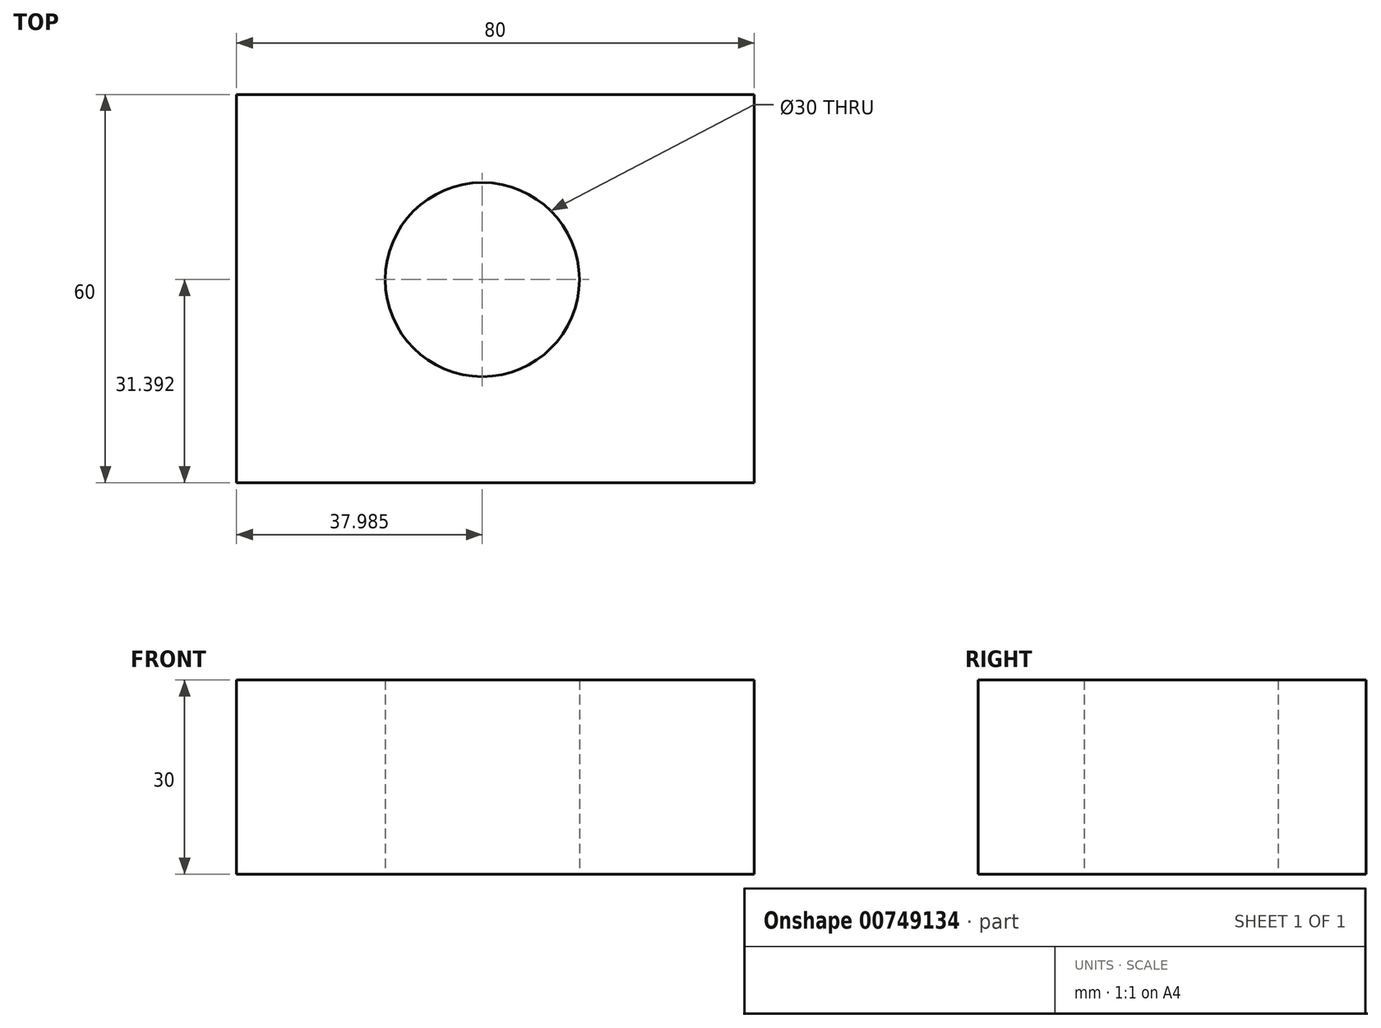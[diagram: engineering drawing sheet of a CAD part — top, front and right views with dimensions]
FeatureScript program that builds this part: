
annotation { "Feature Type Name" : "Feature", "Feature Type Description" : "" }
export const myFeature = defineFeature(function(context is Context, id is Id, definition is map)
    precondition{}
    {
        {
            var Q0;
            Q0=qCreatedBy(makeId("Top.planeOp"),FACE);
            var sketch = newSketch(context, id + "F0", { "sketchPlane" : qUnion([Q0])});
            skLineSegment(sketch, "E0", {"start": v(-63.1, 47.73) * mm, "end": v(-63.1, -12.27) * mm});
            skLineSegment(sketch, "E1", {"start": v(-63.1, -12.27) * mm, "end": v(16.9, -12.27) * mm});
            skLineSegment(sketch, "E2", {"start": v(16.9, -12.27) * mm, "end": v(16.9, 47.73) * mm});
            skLineSegment(sketch, "E3", {"start": v(16.9, 47.73) * mm, "end": v(-63.1, 47.73) * mm});
            skCircle(sketch, "E4", {"center": v(-25.13, 19.12) * mm, "radius": 15 * mm});
            skSolve(sketch);
        }
        {
            var Q0;
            Q0=makeQuery(id+"F0.imprint","IMPRINT",FACE,{"disambiguationData":[TD([[makeQuery(id+"F0.imprint","IMPRINT",EDGE,{"derivedFrom":sQuery(id+"F0.wireOp",EDGE,"E0")}),1.0]])]});
            extrude(context, id + "F1", {"entities" : qUnion([Q0]), "depth" : 30 * mm, "offsetDistance" : 25 * mm});
        }
    });
